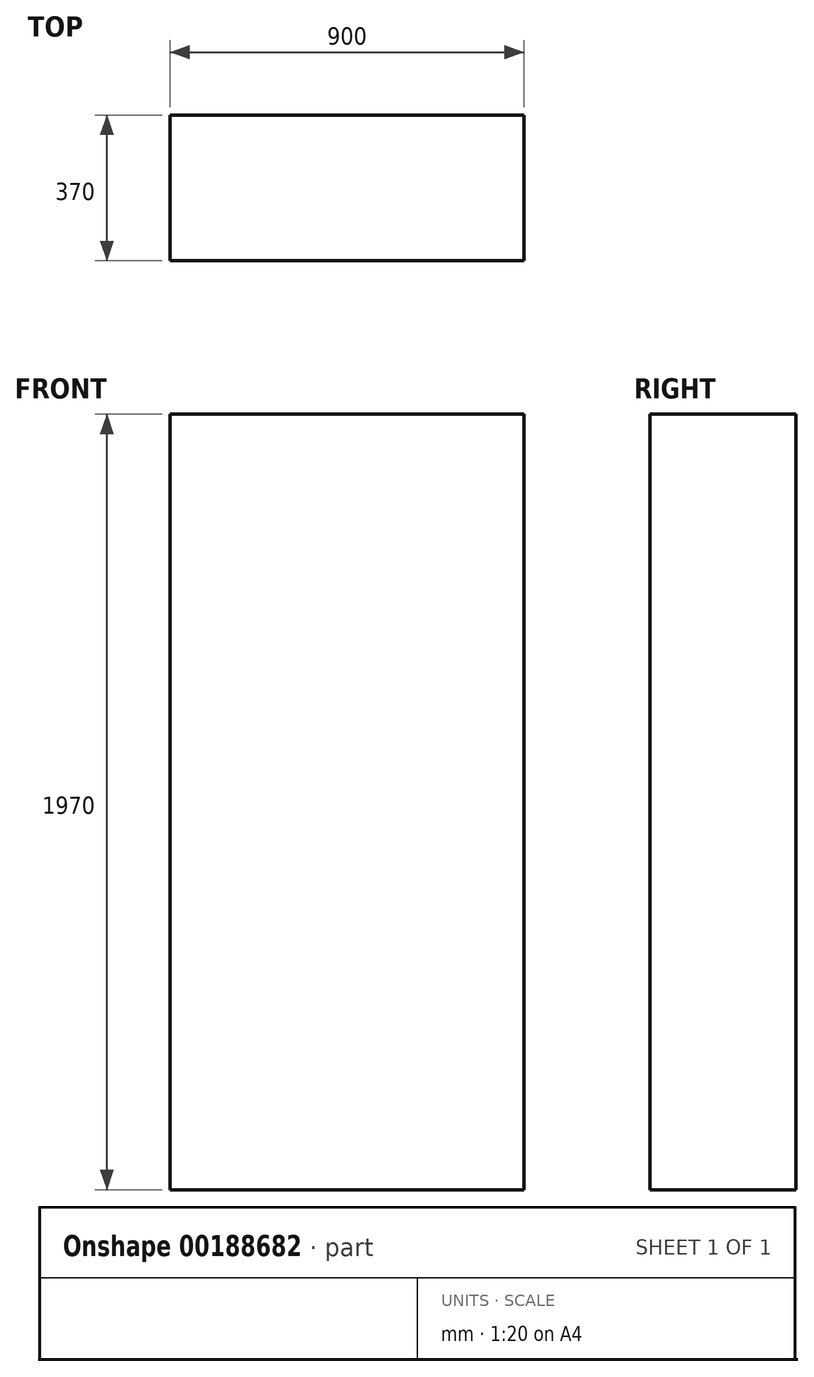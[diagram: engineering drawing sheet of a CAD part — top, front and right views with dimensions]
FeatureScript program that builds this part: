
annotation { "Feature Type Name" : "Feature", "Feature Type Description" : "" }
export const myFeature = defineFeature(function(context is Context, id is Id, definition is map)
    precondition{}
    {
        {
            var Q0;
            Q0=qCreatedBy(makeId("Top.planeOp"),FACE);
            var sketch = newSketch(context, id + "F0", { "sketchPlane" : qUnion([Q0])});
            skLineSegment(sketch, "E0.bottom", {"start": v(450, 185) * mm, "end": v(-450, 185) * mm});
            skLineSegment(sketch, "E0.top", {"start": v(450, -185) * mm, "end": v(-450, -185) * mm});
            skLineSegment(sketch, "E0.left", {"start": v(450, 185) * mm, "end": v(450, -185) * mm});
            skLineSegment(sketch, "E0.right", {"start": v(-450, 185) * mm, "end": v(-450, -185) * mm});
            skPoint(sketch, "E0.middle", {"position": v(0, 0) * mm});
            skSolve(sketch);
        }
        {
            var Q0;
            Q0 = qSketchRegion(id + "F0", true);
            extrude(context, id + "F1", {"entities" : qUnion([Q0]), "depth" : 1970 * mm});
        }
    });
